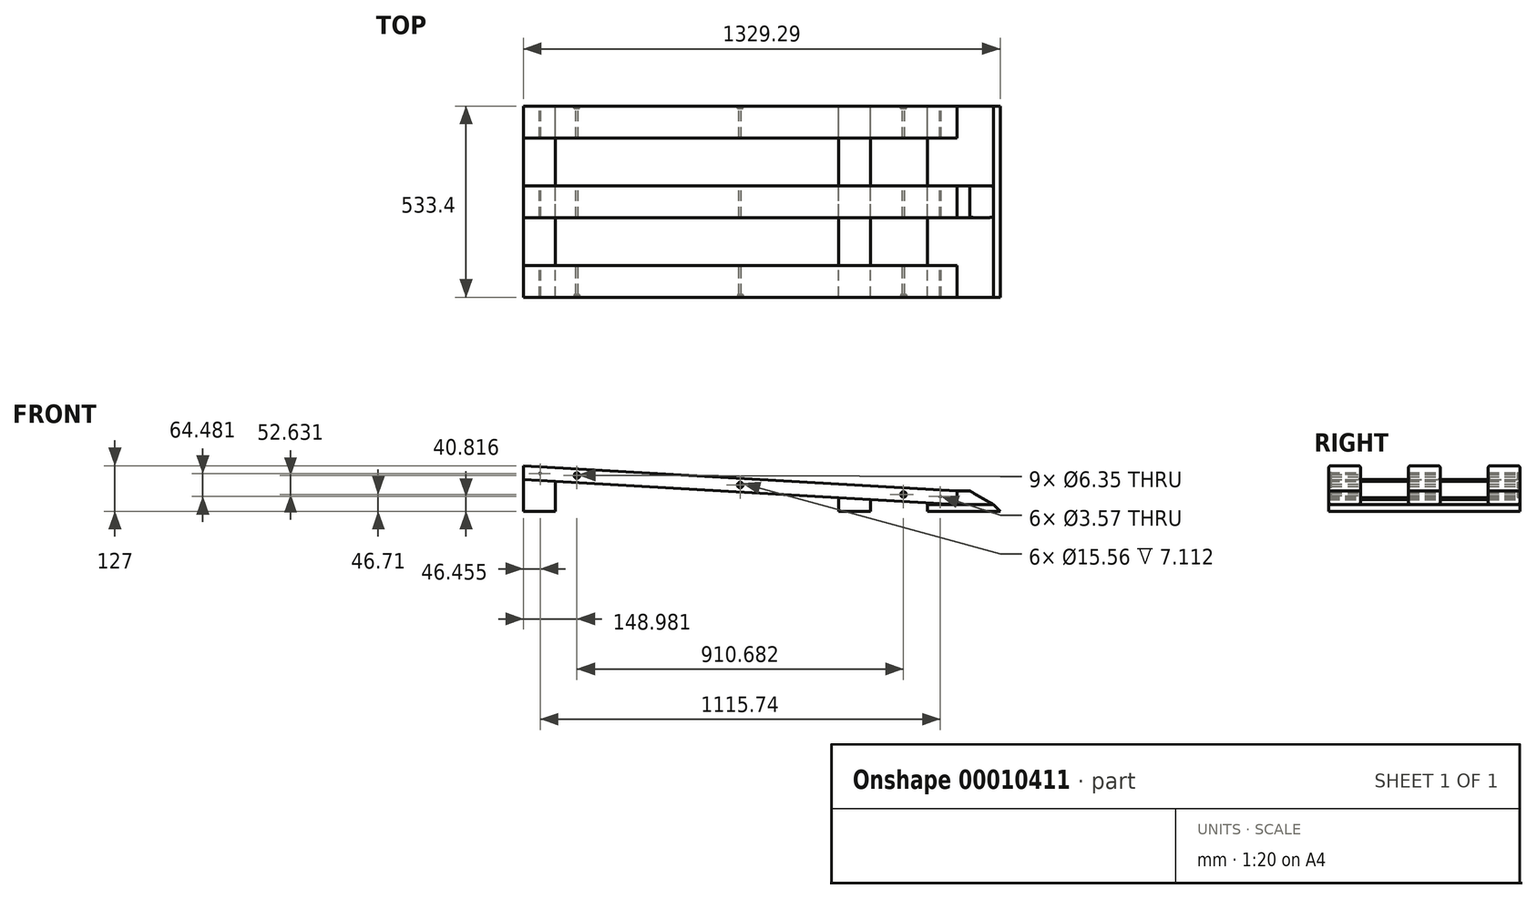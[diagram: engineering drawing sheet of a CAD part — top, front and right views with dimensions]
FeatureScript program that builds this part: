
annotation { "Feature Type Name" : "Feature", "Feature Type Description" : "" }
export const myFeature = defineFeature(function(context is Context, id is Id, definition is map)
    precondition{}
    {
        {
            var Q0;
            Q0=qCreatedBy(makeId("Front.planeOp"),FACE);
            var sketch = newSketch(context, id + "F0", { "sketchPlane" : qUnion([Q0])});
            skLineSegment(sketch, "E0", {"start": v(0, 0) * mm, "end": v(0, 38.1) * mm});
            skLineSegment(sketch, "E1", {"start": v(0, 38.1) * mm, "end": v(35.6, 38.1) * mm});
            skLineSegment(sketch, "E2", {"start": v(35.6, 38.1) * mm, "end": v(101.6, 0) * mm});
            skLineSegment(sketch, "E3", {"start": v(101.6, 0) * mm, "end": v(0, 0) * mm});
            skLineSegment(sketch, "E4", {"start": v(101.6, 0) * mm, "end": v(120.65, -19.05) * mm});
            skLineSegment(sketch, "E5", {"start": v(120.65, -19.05) * mm, "end": v(-82.55, -19.05) * mm});
            skLineSegment(sketch, "E6", {"start": v(-82.55, -19.05) * mm, "end": v(-82.55, 0) * mm});
            skLineSegment(sketch, "E7", {"start": v(-82.55, 0) * mm, "end": v(0, 0) * mm});
            skLineSegment(sketch, "E8", {"start": v(0, 0) * mm, "end": v(-1208.64, 69.85) * mm});
            skLineSegment(sketch, "E9", {"start": v(-1208.64, 69.85) * mm, "end": v(-1208.64, 107.95) * mm});
            skLineSegment(sketch, "E10", {"start": v(-1208.64, 107.95) * mm, "end": v(0, 38.1) * mm});
            skLineSegment(sketch, "E11", {"start": v(-1208.64, 107.95) * mm, "end": v(-1210.83, 69.98) * mm, "construction": true});
            skLineSegment(sketch, "E12", {"start": v(-1210.83, 69.98) * mm, "end": v(-1208.64, 69.85) * mm, "construction": true});
            skLineSegment(sketch, "E13", {"start": v(-1208.64, 69.85) * mm, "end": v(-1208.64, -19.05) * mm, "construction": true});
            skLineSegment(sketch, "E14", {"start": v(-1208.64, -19.05) * mm, "end": v(-72.71, -19.05) * mm, "construction": true});
            skLineSegment(sketch, "E15", {"start": v(-1208.64, 69.85) * mm, "end": v(-1208.64, -19.05) * mm});
            skLineSegment(sketch, "E16", {"start": v(-1119.74, -19.05) * mm, "end": v(-1119.74, 64.71) * mm});
            skLineSegment(sketch, "E17", {"start": v(-1208.64, -19.05) * mm, "end": v(-1119.74, -19.05) * mm});
            skLineSegment(sketch, "E18.right", {"start": v(-329.63, -19.05) * mm, "end": v(-329.63, 19.05) * mm});
            skLineSegment(sketch, "E19", {"start": v(-329.63, -19.05) * mm, "end": v(-240.73, -19.05) * mm});
            skLineSegment(sketch, "E20", {"start": v(-240.73, -19.05) * mm, "end": v(-240.73, 13.91) * mm});
            skLineSegment(sketch, "E21", {"start": v(-603.22, 72.96) * mm, "end": v(-605.41, 34.99) * mm, "construction": true});
            skCircle(sketch, "E22", {"center": v(-604.32, 53.98) * mm, "radius": 3.18 * mm});
            skCircle(sketch, "E23", {"center": v(-1059.66, 80.3) * mm, "radius": 3.18 * mm});
            skLineSegment(sketch, "E24", {"start": v(-1059.66, 99.34) * mm, "end": v(-1059.66, 61.24) * mm, "construction": true});
            skCircle(sketch, "E25.0.MirrorC", {"center": v(-148.98, 27.66) * mm, "radius": 3.18 * mm});
            skCircle(sketch, "E26", {"center": v(-46.45, 21.77) * mm, "radius": 1.79 * mm});
            skCircle(sketch, "E27.0.MirrorC", {"center": v(-1162.18, 86.25) * mm, "radius": 1.79 * mm});
            skSolve(sketch);
        }
        {
            var Q0;
            {var subQ1=sQuery(id+"F0.wireOp",EDGE,"E15");Q0=makeQuery(id+"F0.imprint","IMPRINT",FACE,{"disambiguationData":[TD([[makeQuery(id+"F0.imprint","IMPRINT",EDGE,{"derivedFrom":subQ1}),1.0]])]});}
            var Q1;
            Q1=sQuery(id+"F0.wireOp",EDGE,"E15");
            var Q2;
            Q2=sQuery(id+"F0.wireOp",EDGE,"E17");
            var Q3;
            Q3=sQuery(id+"F0.wireOp",EDGE,"E16");
            var Q4;
            Q4=sQuery(id+"F0.wireOp",EDGE,"E8");
            extrude(context, id + "F1", {"entities" : qUnion([Q0]), "surfaceEntities" : qUnion([Q1, Q2, Q3, Q4]), "endBound" : BoundingType.SYMMETRIC, "depth" : 533.4 * mm, "offsetDistance" : 25.4 * mm});
        }
        {
            var Q0;
            {var subQ1=sQuery(id+"F0.wireOp",EDGE,"E18.right");Q0=makeQuery(id+"F0.imprint","IMPRINT",FACE,{"disambiguationData":[TD([[makeQuery(id+"F0.imprint","IMPRINT",EDGE,{"derivedFrom":subQ1}),-1.0]])]});}
            extrude(context, id + "F2", {"entities" : qUnion([Q0]), "endBound" : BoundingType.SYMMETRIC, "depth" : 533.4 * mm, "offsetDistance" : 25.4 * mm});
        }
        {
            var Q0;
            {var subQ5=sQuery(id+"F0.wireOp",EDGE,"E0");Q0=makeQuery(id+"F0.imprint","IMPRINT",FACE,{"disambiguationData":[TD([[makeQuery(id+"F0.imprint","IMPRINT",EDGE,{"derivedFrom":subQ5}),1.0]])]});}
            extrude(context, id + "F3", {"entities" : qUnion([Q0]), "endBound" : BoundingType.SYMMETRIC, "depth" : 88.9 * mm, "offsetDistance" : 25.4 * mm});
        }
        {
            var Q0;
            Q0=makeQuery(id+"F0.imprint","IMPRINT",FACE,{"disambiguationData":[TD([[makeQuery(id+"F0.imprint","IMPRINT",EDGE,{"derivedFrom":sQuery(id+"F0.wireOp",EDGE,"E0")}),-1.0]])]});
            extrude(context, id + "F4", {"entities" : qUnion([Q0]), "endBound" : BoundingType.SYMMETRIC, "depth" : 88.9 * mm});
        }
        {
            var Q0;
            Q0=makeQuery(id+"F0.imprint","IMPRINT",FACE,{"disambiguationData":[TD([[makeQuery(id+"F0.imprint","IMPRINT",EDGE,{"derivedFrom":sQuery(id+"F0.wireOp",EDGE,"E3")}),1.0]])]});
            extrude(context, id + "F5", {"entities" : qUnion([Q0]), "endBound" : BoundingType.SYMMETRIC, "depth" : 533.4 * mm});
        }
        {
            var Q0;
            Q0=makeQuery(id+"F3.opExtrude","CAP_EDGE",EDGE,{"disambiguationData":[OSD([sQuery(id+"F0.wireOp",EDGE,"E10")])],"isStart":false});
            var Q1;
            Q1=makeQuery(id+"F3.opExtrude","CAP_EDGE",EDGE,{"disambiguationData":[OSD([sQuery(id+"F0.wireOp",EDGE,"E10")])],"isStart":true});
            var Q2;
            Q2=makeQuery(id+"F3.opExtrude","CAP_EDGE",EDGE,{"disambiguationData":[OSD([sQuery(id+"F0.wireOp",EDGE,"E8")])],"isStart":false});
            var Q3;
            Q3=makeQuery(id+"F3.opExtrude","CAP_EDGE",EDGE,{"disambiguationData":[OSD([sQuery(id+"F0.wireOp",EDGE,"E8")])],"isStart":true});
            fillet(context, id + "F6", {"entities" : qUnion([Q0, Q1, Q2, Q3]), "radius" : 6.35 * mm, "allowEdgeOverflow" : false});
        }
        {
            var Q0;
            Q0=makeQuery(id+"F4.opExtrude","CAP_EDGE",EDGE,{"disambiguationData":[OSD([sQuery(id+"F0.wireOp",EDGE,"E1")])],"isStart":false});
            var Q1;
            Q1=makeQuery(id+"F4.opExtrude","CAP_EDGE",EDGE,{"disambiguationData":[OSD([sQuery(id+"F0.wireOp",EDGE,"E3")])],"isStart":false});
            var Q2;
            Q2=makeQuery(id+"F4.opExtrude","CAP_EDGE",EDGE,{"disambiguationData":[OSD([sQuery(id+"F0.wireOp",EDGE,"E1")])],"isStart":true});
            var Q3;
            Q3=makeQuery(id+"F4.opExtrude","CAP_EDGE",EDGE,{"disambiguationData":[OSD([sQuery(id+"F0.wireOp",EDGE,"E3")])],"isStart":true});
            fillet(context, id + "F7", {"entities" : qUnion([Q0, Q1, Q2, Q3]), "radius" : 6.35 * mm, "allowEdgeOverflow" : false});
        }
        {
            var Q0;
            Q0=makeQuery(id+"F3.opExtrude","SWEPT_BODY",BODY,{"disambiguationData":[OSD([sQuery(id+"F0.wireOp",EDGE,"E0"),sQuery(id+"F0.wireOp",EDGE,"E8"),sQuery(id+"F0.wireOp",EDGE,"E9"),sQuery(id+"F0.wireOp",EDGE,"E10"),sQuery(id+"F0.wireOp",EDGE,"E22")])]});
            transform(context, id + "F8", {"entities" : qUnion([Q0]), "transformType" : TransformType.TRANSLATION_3D, "dx" : 0 * mm, "dy" : 222.25 * mm, "dz" : 0 * mm, "makeCopy" : true});
        }
        {
            var Q0;
            Q0=makeQuery(id+"F3.opExtrude","SWEPT_BODY",BODY,{"disambiguationData":[OSD([sQuery(id+"F0.wireOp",EDGE,"E0"),sQuery(id+"F0.wireOp",EDGE,"E8"),sQuery(id+"F0.wireOp",EDGE,"E9"),sQuery(id+"F0.wireOp",EDGE,"E10"),sQuery(id+"F0.wireOp",EDGE,"E22")])]});
            transform(context, id + "F9", {"entities" : qUnion([Q0]), "transformType" : TransformType.TRANSLATION_3D, "dx" : 0 * mm, "dy" : -222.25 * mm, "dz" : 0 * mm, "makeCopy" : true});
        }
        {
            var Q0;
            Q0=makeQuery(id+"F8.opPattern","COPY",FACE,{"derivedFrom":makeQuery(id+"F3.opExtrude","CAP_FACE",FACE,{"disambiguationData":[OSD([sQuery(id+"F0.wireOp",EDGE,"E0"),sQuery(id+"F0.wireOp",EDGE,"E8"),sQuery(id+"F0.wireOp",EDGE,"E9"),sQuery(id+"F0.wireOp",EDGE,"E10"),sQuery(id+"F0.wireOp",EDGE,"E22"),sQuery(id+"F0.wireOp",EDGE,"E23"),sQuery(id+"F0.wireOp",EDGE,"E25.0.MirrorC")])],"isStart":true}),"instanceName":"1"});
            var sketch = newSketch(context, id + "F10", { "sketchPlane" : qUnion([Q0])});
            skCircle(sketch, "E28", {"center": v(148.98, 27.66) * mm, "radius": 7.78 * mm});
            skCircle(sketch, "E29", {"center": v(604.32, 53.98) * mm, "radius": 7.78 * mm});
            skCircle(sketch, "E30", {"center": v(1059.66, 80.3) * mm, "radius": 7.78 * mm});
            skSolve(sketch);
        }
        {
            var Q0;
            Q0 = qSketchRegion(id + "F10", true);
            extrude(context, id + "F11", {"entities" : qUnion([Q0]), "operationType" : NewBodyOperationType.REMOVE, "oppositeDirection" : true, "depth" : 7.11 * mm});
        }
        {
            var Q0;
            Q0=makeQuery(id+"F9.opPattern","COPY",FACE,{"derivedFrom":makeQuery(id+"F3.opExtrude","CAP_FACE",FACE,{"disambiguationData":[OSD([sQuery(id+"F0.wireOp",EDGE,"E0"),sQuery(id+"F0.wireOp",EDGE,"E8"),sQuery(id+"F0.wireOp",EDGE,"E9"),sQuery(id+"F0.wireOp",EDGE,"E10"),sQuery(id+"F0.wireOp",EDGE,"E22"),sQuery(id+"F0.wireOp",EDGE,"E23"),sQuery(id+"F0.wireOp",EDGE,"E25.0.MirrorC")])],"isStart":false}),"instanceName":"1"});
            var sketch = newSketch(context, id + "F12", { "sketchPlane" : qUnion([Q0])});
            skCircle(sketch, "E31", {"center": v(-1059.66, 80.3) * mm, "radius": 7.78 * mm});
            skCircle(sketch, "E32", {"center": v(-604.32, 53.98) * mm, "radius": 7.78 * mm});
            skCircle(sketch, "E33", {"center": v(-148.98, 27.66) * mm, "radius": 7.78 * mm});
            skSolve(sketch);
        }
        {
            var Q0;
            Q0 = qSketchRegion(id + "F12", true);
            extrude(context, id + "F13", {"entities" : qUnion([Q0]), "operationType" : NewBodyOperationType.REMOVE, "oppositeDirection" : true, "depth" : 7.11 * mm});
        }
    });
